# Revit family: 511_2H_PW_nailfin
name_source: partatom
category: Windows
revit_build: Autodesk Revit 2016 (Build: 20150220_1215(x64)
units: mm (PartAtom-declared; Revit-internal decimal feet)

## family parameters
Always vertical = Yes
Cut with Voids When Loaded = No
Host = Wall
OmniClass Number = 23.30.20.00
OmniClass Title = Windows
Room Calculation Point = No
Shared = No

## types (139) — shared parameters
Default Sill Height = 31 1/2"
Rough Height = 2 5/16"
Wall Closure = By host

## per-type parameters (varying)
| type | Bar set | Height | MLH | MLW | MLW2 | Width |
| 72x36 | 36" | 36" | 18" | 4 1/2" | 3" | 72" |
| 48x24 | 24" | 24" | 12" | 3" | 2" | 48" |
| 24x12Min | 12" | 12" | 6" | 1 1/2" | 1" | 24" |
| 120x72Max | 60" | 72" | 36" | 9" | 6" | 120" |
| 108x54 | 54" | 54" | 27" | 6 3/4" | 4 1/2" | 108" |
| 96x48 | 48" | 48" | 24" | 6" | 4" | 96" |
| 84x42 | 42" | 42" | 21" | 5 1/4" | 3 1/2" | 84" |
| 60x30 | 30" | 30" | 15" | 3 3/4" | 2 1/2" | 60" |
| 36x18 | 18" | 18" | 9" | 2 1/4" | 1 1/2" | 36" |
| 24x18 | 12" | 18" | 9" | 2 1/4" | 1 1/2" | 24" |
| 24x24 | 12" | 24" | 12" | 3" | 2" | 24" |
| 24x30 | 12" | 30" | 15" | 3 3/4" | 2 1/2" | 24" |
| 24x36 | 12" | 36" | 18" | 4 1/2" | 3" | 24" |
| 24x42 | 12" | 42" | 21" | 5 1/4" | 3 1/2" | 24" |
| 24x48 | 12" | 48" | 24" | 6" | 4" | 24" |
| 24x54 | 12" | 54" | 27" | 6 3/4" | 4 1/2" | 24" |
| 36x12 | 18" | 12" | 6" | 1 1/2" | 1" | 36" |
| 30x12 | 15" | 12" | 6" | 1 1/2" | 1" | 30" |
| 30x18 | 15" | 18" | 9" | 2 1/4" | 1 1/2" | 30" |
| 30x24 | 15" | 24" | 12" | 3" | 2" | 30" |
| 30x30 | 15" | 30" | 15" | 3 3/4" | 2 1/2" | 30" |
| 30x36 | 15" | 36" | 18" | 4 1/2" | 3" | 30" |
| 30x42 | 15" | 42" | 21" | 5 1/4" | 3 1/2" | 30" |
| 30x48 | 15" | 48" | 24" | 6" | 4" | 30" |
| 30x54 | 15" | 54" | 27" | 6 3/4" | 4 1/2" | 30" |
| 30x60 | 15" | 60" | 30" | 7 1/2" | 5" | 30" |
| 36x24 | 18" | 24" | 12" | 3" | 2" | 36" |
| 36x30 | 18" | 30" | 15" | 3 3/4" | 2 1/2" | 36" |
| 36x36 | 18" | 36" | 18" | 4 1/2" | 3" | 36" |
| 36x42 | 18" | 42" | 21" | 5 1/4" | 3 1/2" | 36" |
| 36x48 | 18" | 48" | 24" | 6" | 4" | 36" |
| 36x54 | 18" | 54" | 27" | 6 3/4" | 4 1/2" | 36" |
| 36x60 | 18" | 60" | 30" | 7 1/2" | 5" | 36" |
| 36x66 | 18" | 66" | 33" | 8 1/4" | 5 1/2" | 36" |
| 42x24 | 21" | 24" | 12" | 3" | 2" | 42" |
| 42x12 | 21" | 12" | 6" | 1 1/2" | 1" | 42" |
| 42x18 | 21" | 18" | 9" | 2 1/4" | 1 1/2" | 42" |
| 42x30 | 21" | 30" | 15" | 3 3/4" | 2 1/2" | 42" |
| 42x36 | 21" | 36" | 18" | 4 1/2" | 3" | 42" |
| 42x42 | 21" | 42" | 21" | 5 1/4" | 3 1/2" | 42" |
| 42x48 | 21" | 48" | 24" | 6" | 4" | 42" |
| 42x54 | 21" | 54" | 27" | 6 3/4" | 4 1/2" | 42" |
| 42x60 | 21" | 60" | 30" | 7 1/2" | 5" | 42" |
| 42x66 | 21" | 66" | 33" | 8 1/4" | 5 1/2" | 42" |
| 42x72 | 21" | 72" | 36" | 9" | 6" | 42" |
| 48x12 | 24" | 12" | 6" | 1 1/2" | 1" | 48" |
| 48x18 | 24" | 18" | 9" | 2 1/4" | 1 1/2" | 48" |
| 48x30 | 24" | 30" | 15" | 3 3/4" | 2 1/2" | 48" |
| 48x36 | 24" | 36" | 18" | 4 1/2" | 3" | 48" |
| 48x42 | 24" | 42" | 21" | 5 1/4" | 3 1/2" | 48" |
| 48x48 | 24" | 48" | 24" | 6" | 4" | 48" |
| 48x54 | 24" | 54" | 27" | 6 3/4" | 4 1/2" | 48" |
| 48x60 | 24" | 60" | 30" | 7 1/2" | 5" | 48" |
| 48x66 | 24" | 66" | 33" | 8 1/4" | 5 1/2" | 48" |
| 48x72 | 24" | 72" | 36" | 9" | 6" | 48" |
| 54x18 | 27" | 18" | 9" | 2 1/4" | 1 1/2" | 54" |
| 54x24 | 27" | 24" | 12" | 3" | 2" | 54" |
| 54x30 | 27" | 30" | 15" | 3 3/4" | 2 1/2" | 54" |
| 54x36 | 27" | 36" | 18" | 4 1/2" | 3" | 54" |
| 54x42 | 27" | 42" | 21" | 5 1/4" | 3 1/2" | 54" |
| 54x48 | 27" | 48" | 24" | 6" | 4" | 54" |
| 54x54 | 27" | 54" | 27" | 6 3/4" | 4 1/2" | 54" |
| 54x60 | 27" | 60" | 30" | 7 1/2" | 5" | 54" |
| 54x66 | 27" | 66" | 33" | 8 1/4" | 5 1/2" | 54" |
| 54x72 | 27" | 72" | 36" | 9" | 6" | 54" |
| 60x24 | 30" | 24" | 12" | 3" | 2" | 60" |
| 60x36 | 30" | 36" | 18" | 4 1/2" | 3" | 60" |
| 60x42 | 30" | 42" | 21" | 5 1/4" | 3 1/2" | 60" |
| 60x48 | 30" | 48" | 24" | 6" | 4" | 60" |
| 60x54 | 30" | 54" | 27" | 6 3/4" | 4 1/2" | 60" |
| 60x60 | 30" | 60" | 30" | 7 1/2" | 5" | 60" |
| 60x66 | 30" | 66" | 33" | 8 1/4" | 5 1/2" | 60" |
| 60x72 | 30" | 72" | 36" | 9" | 6" | 60" |
| 66x30 | 33" | 30" | 15" | 3 3/4" | 2 1/2" | 66" |
| 66x36 | 33" | 36" | 18" | 4 1/2" | 3" | 66" |
| 66x42 | 33" | 42" | 21" | 5 1/4" | 3 1/2" | 66" |
| 66x48 | 33" | 48" | 24" | 6" | 4" | 66" |
| 66x54 | 33" | 54" | 27" | 6 3/4" | 4 1/2" | 66" |
| 66x60 | 33" | 60" | 30" | 7 1/2" | 5" | 66" |
| 66x66 | 33" | 66" | 33" | 8 1/4" | 5 1/2" | 66" |
| 66x72 | 33" | 72" | 36" | 9" | 6" | 66" |
| 72x42 | 36" | 42" | 21" | 5 1/4" | 3 1/2" | 72" |
| 72x48 | 36" | 48" | 24" | 6" | 4" | 72" |
| 72x54 | 36" | 54" | 27" | 6 3/4" | 4 1/2" | 72" |
| 72x60 | 36" | 60" | 30" | 7 1/2" | 5" | 72" |
| 72x66 | 36" | 66" | 33" | 8 1/4" | 5 1/2" | 72" |
| 72x72 | 36" | 72" | 36" | 9" | 6" | 72" |
| 78x36 | 39" | 36" | 18" | 4 1/2" | 3" | 78" |
| 78x42 | 39" | 42" | 21" | 5 1/4" | 3 1/2" | 78" |
| 78x48 | 39" | 48" | 24" | 6" | 4" | 78" |
| 78x54 | 39" | 54" | 27" | 6 3/4" | 4 1/2" | 78" |
| 78x60 | 39" | 60" | 30" | 7 1/2" | 5" | 78" |
| 78x66 | 39" | 66" | 33" | 8 1/4" | 5 1/2" | 78" |
| 78x72 | 39" | 72" | 36" | 9" | 6" | 78" |
| 84x36 | 42" | 36" | 18" | 4 1/2" | 3" | 84" |
| 84x48 | 42" | 48" | 24" | 6" | 4" | 84" |
| 84x54 | 42" | 54" | 27" | 6 3/4" | 4 1/2" | 84" |
| 84x60 | 42" | 60" | 30" | 7 1/2" | 5" | 84" |
| 84x66 | 42" | 66" | 33" | 8 1/4" | 5 1/2" | 84" |
| 84x72 | 42" | 72" | 36" | 9" | 6" | 84" |
| 90x36 | 45" | 36" | 18" | 4 1/2" | 3" | 90" |
| 90x42 | 45" | 42" | 21" | 5 1/4" | 3 1/2" | 90" |
| 90x48 | 45" | 48" | 24" | 6" | 4" | 90" |
| 90x54 | 45" | 54" | 27" | 6 3/4" | 4 1/2" | 90" |
| 90x60 | 45" | 60" | 30" | 7 1/2" | 5" | 90" |
| 90x66 | 45" | 66" | 33" | 8 1/4" | 5 1/2" | 90" |
| 90x72 | 45" | 72" | 36" | 9" | 6" | 90" |
| 96x36 | 48" | 36" | 18" | 4 1/2" | 3" | 96" |
| 96x42 | 48" | 42" | 21" | 5 1/4" | 3 1/2" | 96" |
| 96x54 | 48" | 54" | 27" | 6 3/4" | 4 1/2" | 96" |
| 96x60 | 48" | 60" | 30" | 7 1/2" | 5" | 96" |
| 96x66 | 48" | 66" | 33" | 8 1/4" | 5 1/2" | 96" |
| 96x72 | 48" | 72" | 36" | 9" | 6" | 96" |
| 102x36 | 51" | 36" | 18" | 4 1/2" | 3" | 102" |
| 102x42 | 51" | 42" | 21" | 5 1/4" | 3 1/2" | 102" |
| 102x48 | 51" | 48" | 24" | 6" | 4" | 102" |
| 102x54 | 51" | 54" | 27" | 6 3/4" | 4 1/2" | 102" |
| 102x60 | 51" | 60" | 30" | 7 1/2" | 5" | 102" |
| 102x66 | 51" | 66" | 33" | 8 1/4" | 5 1/2" | 102" |
| 102x72 | 51" | 72" | 36" | 9" | 6" | 102" |
| 108x36 | 54" | 36" | 18" | 4 1/2" | 3" | 108" |
| 108x42 | 54" | 42" | 21" | 5 1/4" | 3 1/2" | 108" |
| 108x48 | 54" | 48" | 24" | 6" | 4" | 108" |
| 108x60 | 54" | 60" | 30" | 7 1/2" | 5" | 108" |
| 108x66 | 54" | 66" | 33" | 8 1/4" | 5 1/2" | 108" |
| 108x72 | 54" | 72" | 36" | 9" | 6" | 108" |
| 114x36 | 57" | 36" | 18" | 4 1/2" | 3" | 114" |
| 114x42 | 57" | 42" | 21" | 5 1/4" | 3 1/2" | 114" |
| 114x48 | 57" | 48" | 24" | 6" | 4" | 114" |
| 114x54 | 57" | 54" | 27" | 6 3/4" | 4 1/2" | 114" |
| 114x60 | 57" | 60" | 30" | 7 1/2" | 5" | 114" |
| 114x66 | 57" | 66" | 33" | 8 1/4" | 5 1/2" | 114" |
| 114x72 | 57" | 72" | 36" | 9" | 6" | 114" |
| 120x36 | 60" | 36" | 18" | 4 1/2" | 3" | 120" |
| 120x42 | 60" | 42" | 21" | 5 1/4" | 3 1/2" | 120" |
| 120x48 | 60" | 48" | 24" | 6" | 4" | 120" |
| 120x54 | 60" | 54" | 27" | 6 3/4" | 4 1/2" | 120" |
| 120x60 | 60" | 60" | 30" | 7 1/2" | 5" | 120" |
| 120x66 | 60" | 66" | 33" | 8 1/4" | 5 1/2" | 120" |

## geometry (parser evidence)
native form markers: Sweep x6
no freeform markers — native parametric forms only
